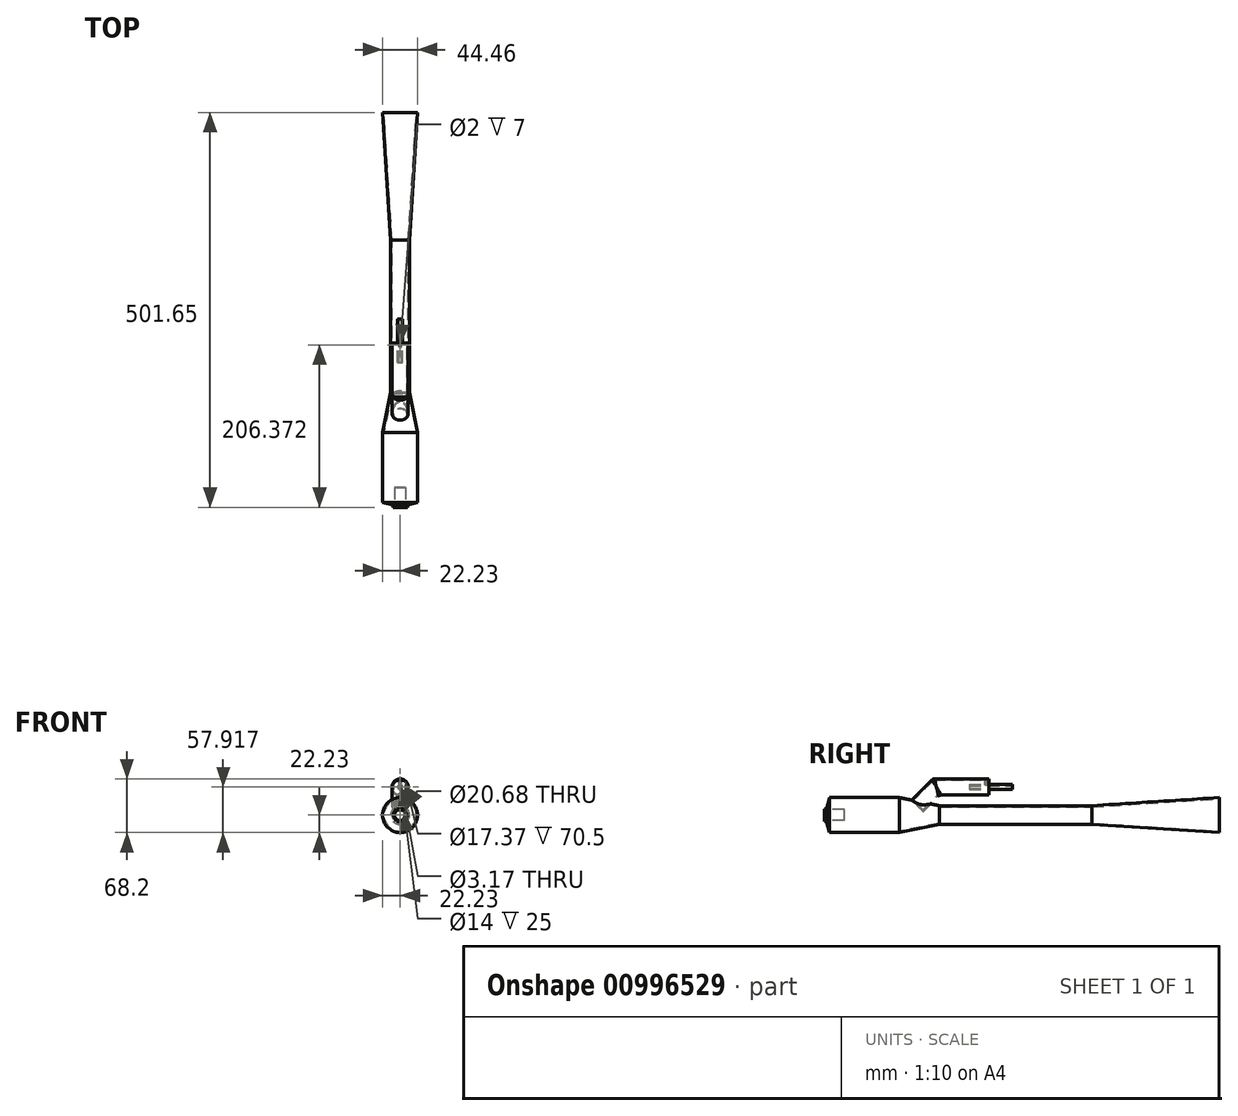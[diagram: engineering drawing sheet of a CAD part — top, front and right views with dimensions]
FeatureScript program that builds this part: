
annotation { "Feature Type Name" : "Feature", "Feature Type Description" : "" }
export const myFeature = defineFeature(function(context is Context, id is Id, definition is map)
    precondition{}
    {
        {
            var Q0;
            Q0=qCreatedBy(makeId("Right.planeOp"),FACE);
            var sketch = newSketch(context, id + "F0", { "sketchPlane" : qUnion([Q0])});
            skLineSegment(sketch, "E0.bottom", {"start": v(-341.31, 0) * mm, "end": v(341.31, 0) * mm, "construction": true});
            skLineSegment(sketch, "E0.top", {"start": v(-341.31, 22.23) * mm, "end": v(341.31, 22.22) * mm});
            skLineSegment(sketch, "E0.left", {"start": v(-341.31, 0) * mm, "end": v(-341.31, 22.23) * mm});
            skLineSegment(sketch, "E0.right", {"start": v(341.31, 0) * mm, "end": v(341.31, 22.23) * mm});
            skLineSegment(sketch, "E1", {"start": v(341.31, 0) * mm, "end": v(-341.31, 0) * mm});
            skLineSegment(sketch, "E2.bottom", {"start": v(-341.31, 0) * mm, "end": v(-338.14, 0) * mm});
            skLineSegment(sketch, "E2.top", {"start": v(-341.31, 22.23) * mm, "end": v(-338.14, 22.23) * mm});
            skLineSegment(sketch, "E2.right", {"start": v(-338.14, 0) * mm, "end": v(-338.14, 22.23) * mm});
            skLineSegment(sketch, "E3.bottom", {"start": v(341.31, 0) * mm, "end": v(163.51, 0) * mm});
            skLineSegment(sketch, "E3.top", {"start": v(341.31, 22.22) * mm, "end": v(163.51, 22.22) * mm});
            skLineSegment(sketch, "E3.left", {"start": v(341.31, 0) * mm, "end": v(341.31, 22.22) * mm});
            skLineSegment(sketch, "E3.right", {"start": v(163.51, 0) * mm, "end": v(163.51, 22.22) * mm});
            skLineSegment(sketch, "E4.bottom", {"start": v(163.51, 22.22) * mm, "end": v(1.59, 22.22) * mm, "construction": true});
            skLineSegment(sketch, "E4.top", {"start": v(163.51, 0) * mm, "end": v(1.59, 0) * mm});
            skLineSegment(sketch, "E4.left", {"start": v(163.51, 22.22) * mm, "end": v(163.51, 0) * mm});
            skLineSegment(sketch, "E4.right", {"start": v(1.59, 22.22) * mm, "end": v(1.59, 0) * mm});
            skLineSegment(sketch, "E5.bottom", {"start": v(1.59, 0) * mm, "end": v(-192.09, 0) * mm});
            skLineSegment(sketch, "E5.top", {"start": v(1.59, 22.23) * mm, "end": v(-192.09, 22.23) * mm, "construction": true});
            skLineSegment(sketch, "E5.left", {"start": v(1.59, 0) * mm, "end": v(1.59, 22.23) * mm});
            skLineSegment(sketch, "E5.right", {"start": v(-192.09, 0) * mm, "end": v(-192.09, 22.23) * mm, "construction": true});
            skLineSegment(sketch, "E6.bottom", {"start": v(-192.09, 0) * mm, "end": v(-242.89, 0) * mm});
            skLineSegment(sketch, "E6.top", {"start": v(-192.09, 22.23) * mm, "end": v(-242.89, 22.23) * mm, "construction": true});
            skLineSegment(sketch, "E6.left", {"start": v(-192.09, 0) * mm, "end": v(-192.09, 22.23) * mm});
            skLineSegment(sketch, "E6.right", {"start": v(-242.89, 0) * mm, "end": v(-242.89, 22.23) * mm, "construction": true});
            skLineSegment(sketch, "E7.bottom", {"start": v(-242.89, 0) * mm, "end": v(-331.79, 0) * mm});
            skLineSegment(sketch, "E7.top", {"start": v(-242.89, 22.23) * mm, "end": v(-331.79, 22.23) * mm});
            skLineSegment(sketch, "E7.left", {"start": v(-242.89, 0) * mm, "end": v(-242.89, 22.23) * mm});
            skLineSegment(sketch, "E7.right", {"start": v(-331.79, 0) * mm, "end": v(-331.79, 22.23) * mm, "construction": true});
            skLineSegment(sketch, "E8", {"start": v(-331.79, 22.23) * mm, "end": v(-338.14, 0) * mm});
            skLineSegment(sketch, "E9", {"start": v(1.59, 11.94) * mm, "end": v(-192.09, 11.94) * mm});
            skLineSegment(sketch, "E10", {"start": v(-242.89, 22.23) * mm, "end": v(-192.09, 11.94) * mm});
            skLineSegment(sketch, "E11", {"start": v(1.59, 11.94) * mm, "end": v(163.51, 22.22) * mm});
            skLineSegment(sketch, "E12", {"start": v(-336.47, 0) * mm, "end": v(-330.12, 22.23) * mm});
            skLineSegment(sketch, "E13", {"start": v(-332.24, 20.63) * mm, "end": v(-242.89, 20.63) * mm});
            skLineSegment(sketch, "E14", {"start": v(-242.89, 20.63) * mm, "end": v(-192.09, 10.34) * mm});
            skLineSegment(sketch, "E15", {"start": v(-192.09, 10.34) * mm, "end": v(1.59, 10.34) * mm});
            skLineSegment(sketch, "E16", {"start": v(1.59, 10.34) * mm, "end": v(163.51, 20.62) * mm});
            skLineSegment(sketch, "E17", {"start": v(163.51, 20.62) * mm, "end": v(341.31, 20.62) * mm});
            skLineSegment(sketch, "E18", {"start": v(-227.33, 19.07) * mm, "end": v(-206.94, 39.46) * mm});
            skLineSegment(sketch, "E19", {"start": v(-206.94, 39.46) * mm, "end": v(-192.4, 24.92) * mm});
            skLineSegment(sketch, "E20", {"start": v(-192.4, 24.92) * mm, "end": v(-203.13, 14.17) * mm});
            skLineSegment(sketch, "E21", {"start": v(-192.4, 24.92) * mm, "end": v(-192.4, 46.02) * mm, "construction": true});
            skLineSegment(sketch, "E22", {"start": v(-192.4, 46.02) * mm, "end": v(-129.27, 46.02) * mm});
            skLineSegment(sketch, "E23", {"start": v(-129.27, 46.02) * mm, "end": v(-129.27, 24.92) * mm});
            skLineSegment(sketch, "E24", {"start": v(-129.27, 24.92) * mm, "end": v(-192.4, 24.92) * mm});
            skLineSegment(sketch, "E25", {"start": v(-206.94, 39.46) * mm, "end": v(-200.39, 46.02) * mm});
            skLineSegment(sketch, "E26", {"start": v(-200.39, 46.02) * mm, "end": v(-192.4, 46.02) * mm});
            skLineSegment(sketch, "E27", {"start": v(-200.39, 46.02) * mm, "end": v(-192.4, 24.92) * mm});
            skLineSegment(sketch, "E28", {"start": v(-200.39, 46.02) * mm, "end": v(-203.19, 53.4) * mm});
            skLineSegment(sketch, "E29", {"start": v(-200.39, 46.02) * mm, "end": v(-207.92, 46.02) * mm});
            skLineSegment(sketch, "E30", {"start": v(-225.45, 18.7) * mm, "end": v(-205.8, 38.33) * mm});
            skLineSegment(sketch, "E31", {"start": v(-205.8, 38.33) * mm, "end": v(-199.77, 44.37) * mm});
            skLineSegment(sketch, "E32", {"start": v(-199.77, 44.37) * mm, "end": v(-129.27, 44.37) * mm});
            skLineSegment(sketch, "E33", {"start": v(-129.27, 26.52) * mm, "end": v(-192.4, 26.52) * mm});
            skLineSegment(sketch, "E34", {"start": v(-192.4, 26.52) * mm, "end": v(-193, 26.52) * mm});
            skLineSegment(sketch, "E35", {"start": v(-193, 26.52) * mm, "end": v(-204.97, 14.55) * mm});
            skLineSegment(sketch, "E36", {"start": v(-199.67, 32.19) * mm, "end": v(-215.23, 16.62) * mm, "construction": true});
            skLineSegment(sketch, "E37", {"start": v(-199.67, 32.19) * mm, "end": v(-196.39, 35.47) * mm, "construction": true});
            skLineSegment(sketch, "E38", {"start": v(-196.39, 35.47) * mm, "end": v(-129.27, 35.47) * mm, "construction": true});
            skLineSegment(sketch, "E39", {"start": v(-199.77, 44.37) * mm, "end": v(-200.9, 45.5) * mm});
            skSolve(sketch);
        }
        {
            var Q0;
            {var subQ0=sQuery(id+"F0.wireOp",EDGE,"E3.top");Q0=makeQuery(id+"F0.imprint","IMPRINT",FACE,{"disambiguationData":[TD([[makeQuery(id+"F0.imprint","IMPRINT",EDGE,{"derivedFrom":subQ0}),1.0]])]});}
            var Q1;
            {var subQ0=sQuery(id+"F0.wireOp",EDGE,"E11");Q1=makeQuery(id+"F0.imprint","IMPRINT",FACE,{"disambiguationData":[TD([[makeQuery(id+"F0.imprint","IMPRINT",EDGE,{"derivedFrom":subQ0}),-1.0]])]});}
            var Q2;
            {var subQ0=sQuery(id+"F0.wireOp",EDGE,"E9");Q2=makeQuery(id+"F0.imprint","IMPRINT",FACE,{"disambiguationData":[TD([[makeQuery(id+"F0.imprint","IMPRINT",EDGE,{"derivedFrom":subQ0}),1.0]])]});}
            var Q3;
            {var subQ5=sQuery(id+"F0.wireOp",EDGE,"E14");Q3=makeQuery(id+"F0.imprint","IMPRINT",FACE,{"disambiguationData":[TD([[makeQuery(id+"F0.imprint","IMPRINT",EDGE,{"derivedFrom":subQ5}),1.0]])]});}
            var Q4;
            {var subQ1=sQuery(id+"F0.wireOp",EDGE,"E7.top");var subQ3=sQuery(id+"F0.wireOp",EDGE,"E12");var subQ4=makeQuery(id+"F0.imprint","INTERSECT",VERTEX,{"derivedFrom":[subQ1,subQ3]});Q4=makeQuery(id+"F0.imprint","IMPRINT",FACE,{"disambiguationData":[TD([[makeQuery(id+"F0.imprint","IMPRINT",EDGE,{"disambiguationData":[TD([[subQ4,1.0]])],"derivedFrom":subQ3}),-1.0]])]});}
            var Q5;
            {var subQ1=sQuery(id+"F0.wireOp",EDGE,"E1");var subQ3=sQuery(id+"F0.wireOp",EDGE,"E12");var subQ4=makeQuery(id+"F0.imprint","INTERSECT",VERTEX,{"derivedFrom":[subQ1,subQ3]});Q5=makeQuery(id+"F0.imprint","IMPRINT",FACE,{"disambiguationData":[TD([[makeQuery(id+"F0.imprint","IMPRINT",EDGE,{"disambiguationData":[TD([[subQ4,-1.0]])],"derivedFrom":subQ3}),1.0]])]});}
            var Q6;
            {var subQ1=sQuery(id+"F0.wireOp",EDGE,"E7.top");var subQ3=sQuery(id+"F0.wireOp",EDGE,"E12");var subQ4=makeQuery(id+"F0.imprint","INTERSECT",VERTEX,{"derivedFrom":[subQ1,subQ3]});Q6=makeQuery(id+"F0.imprint","IMPRINT",FACE,{"disambiguationData":[TD([[makeQuery(id+"F0.imprint","IMPRINT",EDGE,{"disambiguationData":[TD([[subQ4,1.0]])],"derivedFrom":subQ3}),1.0]])]});}
            var Q7;
            Q7=sQuery(id+"F0.wireOp",EDGE,"E1");
            revolve(context, id + "F1", {"surfaceOperationType" : NewSurfaceOperationType.NEW, "entities" : qUnion([Q0, Q1, Q2, Q3, Q4, Q5, Q6]), "axis" : qUnion([Q7]), "revolveType" : RevolveType.FULL});
        }
        {
            var Q0;
            {var subQ0=sQuery(id+"F0.wireOp",EDGE,"E18");var subQ1=sQuery(id+"F0.wireOp",EDGE,"E0.top");var subQ2=makeQuery(id+"F0.imprint","INTERSECT",VERTEX,{"derivedFrom":[subQ1,subQ0]});Q0=makeQuery(id+"F0.imprint","IMPRINT",FACE,{"disambiguationData":[TD([[makeQuery(id+"F0.imprint","IMPRINT",EDGE,{"disambiguationData":[TD([[subQ2,-1.0]])],"derivedFrom":subQ1}),-1.0]])]});}
            var Q1;
            {var subQ0=sQuery(id+"F0.wireOp",EDGE,"E18");var subQ1=sQuery(id+"F0.wireOp",EDGE,"E0.top");var subQ2=makeQuery(id+"F0.imprint","INTERSECT",VERTEX,{"derivedFrom":[subQ1,subQ0]});Q1=makeQuery(id+"F0.imprint","IMPRINT",FACE,{"disambiguationData":[TD([[makeQuery(id+"F0.imprint","IMPRINT",EDGE,{"disambiguationData":[TD([[subQ2,-1.0]])],"derivedFrom":subQ1}),1.0]])]});}
            var Q2;
            Q2=sQuery(id+"F0.wireOp",EDGE,"E36");
            revolve(context, id + "F2", {"operationType" : NewBodyOperationType.ADD, "surfaceOperationType" : NewSurfaceOperationType.NEW, "entities" : qUnion([Q0, Q1]), "axis" : qUnion([Q2]), "revolveType" : RevolveType.FULL});
        }
        {
            var Q0;
            Q0=makeQuery(id+"F2.opRevolve","SWEPT_FACE",FACE,{"disambiguationData":[OSD([sQuery(id+"F0.wireOp",EDGE,"E19")])]});
            var sketch = newSketch(context, id + "F3", { "sketchPlane" : qUnion([Q0])});
            skCircle(sketch, "E40.0", {"center": v(0, 163.95) * mm, "radius": 8.69 * mm});
            skCircle(sketch, "E41.0", {"center": v(0, 163.95) * mm, "radius": 10.29 * mm});
            skSolve(sketch);
        }
        {
            var Q0;
            Q0=makeQuery(id+"F3.imprint","IMPRINT",FACE,{"disambiguationData":[TD([[makeQuery(id+"F3.imprint","IMPRINT",EDGE,{"derivedFrom":sQuery(id+"F3.wireOp",EDGE,"E40.0")}),1.0]])]});
            var Q1;
            Q1=makeQuery(id+"F1.opRevolve","SWEPT_FACE",FACE,{"disambiguationData":[OSD([sQuery(id+"F0.wireOp",EDGE,"E14")])]});
            extrude(context, id + "F4", {"entities" : qUnion([Q0]), "operationType" : NewBodyOperationType.REMOVE, "oppositeDirection" : true, "depth" : 35 * mm, "endBoundEntityFace" : qUnion([Q1]), "offsetDistance" : 25 * mm});
        }
        {
            var Q0;
            Q0=makeQuery(id+"F2.opRevolve","SWEPT_FACE",FACE,{"disambiguationData":[OSD([sQuery(id+"F0.wireOp",EDGE,"E19")])]});
            var Q1;
            Q1=sQuery(id+"F0.wireOp",EDGE,"E31");
            var Q2;
            Q2=sQuery(id+"F0.wireOp",EDGE,"E32");
            sweep(context, id + "F5", {"operationType" : NewBodyOperationType.ADD, "profiles" : qUnion([Q0]), "path" : qUnion([Q1, Q2])});
        }
        {
            var Q0;
            Q0=makeQuery(id+"F5.opSweep","MID_CAP_EDGE",EDGE,{"disambiguationData":[OSD([sQuery(id+"F0.wireOp",VERTEX,"E32.start"),sQuery(id+"F0.wireOp",EDGE,"E18"),sQuery(id+"F0.wireOp",EDGE,"E19"),sQuery(id+"F0.wireOp",EDGE,"E25")])],"capPos":1.0});
            fillet(context, id + "F6", {"entities" : qUnion([Q0]), "radius" : 5 * mm, "tangentPropagation" : true, "allowEdgeOverflow" : false});
        }
        {
            var Q0;
            Q0=makeQuery(id+"F5.opSweep","CAP_FACE",FACE,{"disambiguationData":[OSD([sQuery(id+"F0.wireOp",VERTEX,"E32.end"),sQuery(id+"F0.wireOp",EDGE,"E19")])],"isStart":false});
            var sketch = newSketch(context, id + "F7", { "sketchPlane" : qUnion([Q0])});
            skCircle(sketch, "E42", {"center": v(0, 35.69) * mm, "radius": 1.59 * mm});
            skCircle(sketch, "E43", {"center": v(0, 35.69) * mm, "radius": 3.19 * mm});
            skLineSegment(sketch, "E44.bottom", {"start": v(-1.59, 35.69) * mm, "end": v(1.59, 35.69) * mm});
            skLineSegment(sketch, "E44.left", {"start": v(-1.59, 35.69) * mm, "end": v(-1.59, 44.23) * mm});
            skLineSegment(sketch, "E44.right", {"start": v(1.59, 35.69) * mm, "end": v(1.59, 44.23) * mm});
            skCircle(sketch, "E45.0", {"center": v(0, 35.69) * mm, "radius": 8.69 * mm});
            skSolve(sketch);
        }
        {
            var Q0;
            Q0=makeQuery(id+"F7.imprint","IMPRINT",FACE,{"disambiguationData":[TD([[makeQuery(id+"F7.imprint","IMPRINT",EDGE,{"derivedFrom":sQuery(id+"F7.wireOp",EDGE,"E42")}),-1.0]])]});
            extrude(context, id + "F8", {"entities" : qUnion([Q0]), "oppositeDirection" : true, "depth" : 25 * mm, "offsetDistance" : 25 * mm, "hasSecondDirection" : true, "secondDirectionOppositeDirection" : false, "secondDirectionDepth" : 30 * mm});
        }
        {
            var Q0;
            {var subQ0=sQuery(id+"F7.wireOp",EDGE,"E44.left");var subQ1=sQuery(id+"F7.wireOp",EDGE,"E43");var subQ2=makeQuery(id+"F7.imprint","INTERSECT",VERTEX,{"derivedFrom":[subQ1,subQ0]});Q0=makeQuery(id+"F7.imprint","IMPRINT",FACE,{"disambiguationData":[TD([[makeQuery(id+"F7.imprint","IMPRINT",EDGE,{"disambiguationData":[TD([[subQ2,1.0]])],"derivedFrom":subQ1}),-1.0]])]});}
            extrude(context, id + "F9", {"entities" : qUnion([Q0]), "operationType" : NewBodyOperationType.ADD, "oppositeDirection" : true, "depth" : 5 * mm, "offsetDistance" : 25 * mm});
        }
        {
            var Q0;
            {var subQ0=sQuery(id+"F0.wireOp",EDGE,"E25");var subQ1=sQuery(id+"F0.wireOp",EDGE,"E19");var subQ2=sQuery(id+"F0.wireOp",EDGE,"E18");Q0=makeQuery(id+"F6.opFillet","BLEND_EDGE",EDGE,{"disambiguationData":[OD(0.0)],"blendedFrom":[makeQuery(id+"F5.opSweep","MID_CAP_EDGE",EDGE,{"disambiguationData":[OSD([sQuery(id+"F0.wireOp",VERTEX,"E32.start"),subQ2,subQ1,subQ0])],"capPos":1.0}),makeQuery(id+"F5.opSweep","SWEPT_FACE",FACE,{"disambiguationData":[OSD([subQ2,subQ1,subQ0,sQuery(id+"F0.wireOp",EDGE,"E32")])]})],"blendedInto":[makeQuery(id+"F5.opSweep","SWEPT_FACE",FACE,{"disambiguationData":[OSD([subQ2,subQ1,subQ0,sQuery(id+"F0.wireOp",EDGE,"E32")])]})]});}
            cPoint(context, id + "F10", {"entities" : qUnion([Q0]), "parameter" : 0.5});
        }
        {
            var Q0;
            Q0=qCreatedBy(makeId("Top.planeOp"),FACE);
            var Q1;
            Q1 = qCreatedBy(id + "F10" ,VERTEX);
            cPlane(context, id + "F11", {"entities" : qUnion([Q0, Q1]), "cplaneType" : CPlaneType.PLANE_POINT, "offset" : 50 * mm, "width" : 150 * mm, "height" : 150 * mm});
        }
        {
            var Q0;
            Q0=qCreatedBy(id+"F11.planeOp",FACE);
            var sketch = newSketch(context, id + "F12", { "sketchPlane" : qUnion([Q0])});
            skCircle(sketch, "E46", {"center": v(0, -131.77) * mm, "radius": 1 * mm});
            skSolve(sketch);
        }
        {
            var Q0;
            Q0=makeQuery(id+"F12.imprint","IMPRINT",FACE,{"disambiguationData":[TD([[makeQuery(id+"F12.imprint","IMPRINT",EDGE,{"derivedFrom":sQuery(id+"F12.wireOp",EDGE,"E46")}),1.0]])]});
            extrude(context, id + "F13", {"entities" : qUnion([Q0]), "operationType" : NewBodyOperationType.REMOVE, "oppositeDirection" : true, "depth" : 7 * mm, "offsetDistance" : 25 * mm});
        }
        {
            var Q0;
            Q0=qCreatedBy(makeId("Front.planeOp"),FACE);
            var Q1;
            Q1=makeQuery(id+"F1.opRevolve","SWEPT_VERTEX",VERTEX,{"disambiguationData":[OSD([sQuery(id+"F0.wireOp",EDGE,"E1"),sQuery(id+"F0.wireOp",EDGE,"E2.bottom"),sQuery(id+"F0.wireOp",EDGE,"E2.right"),sQuery(id+"F0.wireOp",EDGE,"E8")])]});
            cPlane(context, id + "F14", {"entities" : qUnion([Q0, Q1]), "cplaneType" : CPlaneType.PLANE_POINT, "offset" : 25 * mm, "width" : 150 * mm, "height" : 150 * mm});
        }
        {
            var Q0;
            Q0=qCreatedBy(id+"F14.planeOp",FACE);
            var sketch = newSketch(context, id + "F15", { "sketchPlane" : qUnion([Q0])});
            skCircle(sketch, "E47", {"center": v(0, 0) * mm, "radius": 7 * mm});
            skSolve(sketch);
        }
        {
            var Q0;
            Q0=makeQuery(id+"F15.imprint","IMPRINT",FACE,{"disambiguationData":[TD([[makeQuery(id+"F15.imprint","IMPRINT",EDGE,{"derivedFrom":sQuery(id+"F15.wireOp",EDGE,"E47")}),1.0]])]});
            extrude(context, id + "F16", {"entities" : qUnion([Q0]), "operationType" : NewBodyOperationType.REMOVE, "oppositeDirection" : true, "depth" : 25 * mm, "offsetDistance" : 25 * mm});
        }
        {
            var Q0;
            Q0=qCreatedBy(id+"F14.planeOp",FACE);
            var sketch = newSketch(context, id + "F17", { "sketchPlane" : qUnion([Q0])});
            skCircle(sketch, "E48.cCircle", {"center": v(0, 0) * mm, "radius": 8 * mm, "construction": true});
            skLineSegment(sketch, "E48.0", {"start": v(9.24, 0) * mm, "end": v(4.62, -8) * mm});
            skLineSegment(sketch, "E48.1", {"start": v(4.62, -8) * mm, "end": v(-4.62, -8) * mm});
            skLineSegment(sketch, "E48.2", {"start": v(-4.62, -8) * mm, "end": v(-9.24, 0) * mm});
            skLineSegment(sketch, "E48.3", {"start": v(-9.24, 0) * mm, "end": v(-4.62, 8) * mm});
            skLineSegment(sketch, "E48.4", {"start": v(-4.62, 8) * mm, "end": v(4.62, 8) * mm});
            skLineSegment(sketch, "E48.5", {"start": v(4.62, 8) * mm, "end": v(9.24, 0) * mm});
            skPoint(sketch, "E48.0.midPoint", {"position": v(6.93, -4) * mm});
            skCircle(sketch, "E49", {"center": v(0, 0) * mm, "radius": 7 * mm});
            skSolve(sketch);
        }
        {
            var Q0;
            Q0=makeQuery(id+"F17.imprint","IMPRINT",FACE,{"disambiguationData":[TD([[makeQuery(id+"F17.imprint","IMPRINT",EDGE,{"derivedFrom":sQuery(id+"F17.wireOp",EDGE,"E48.0")}),-1.0]])]});
            extrude(context, id + "F18", {"entities" : qUnion([Q0]), "operationType" : NewBodyOperationType.ADD, "endBound" : BoundingType.UP_TO_NEXT, "oppositeDirection" : true, "depth" : 25 * mm, "offsetDistance" : 25 * mm});
        }
    });
